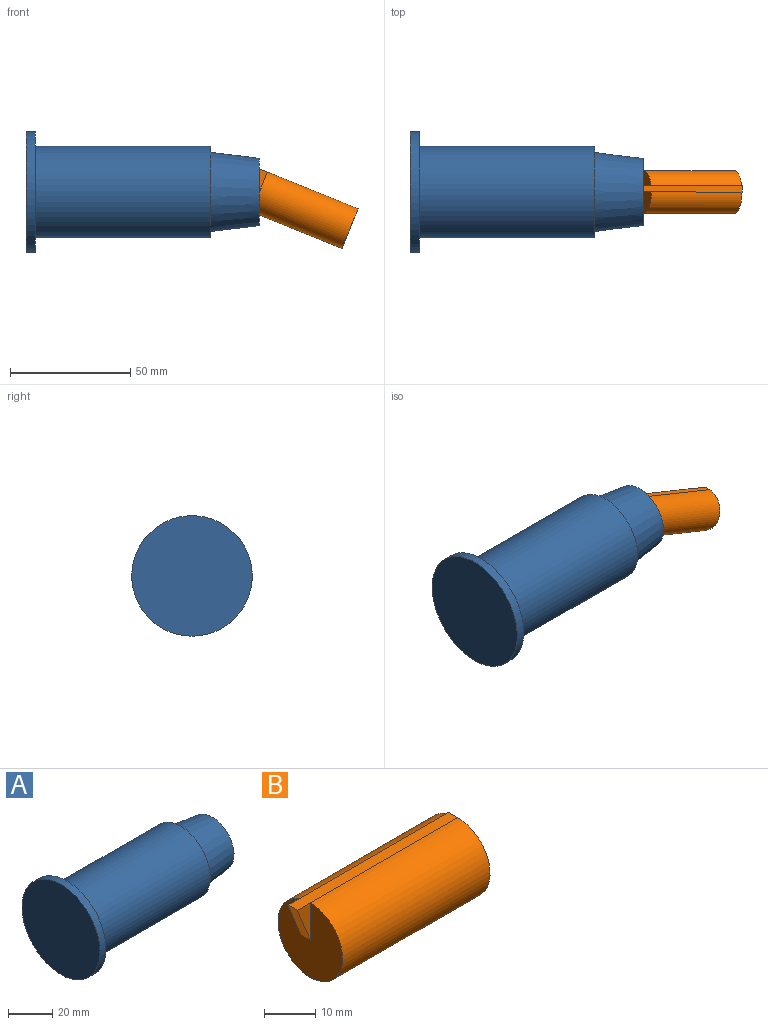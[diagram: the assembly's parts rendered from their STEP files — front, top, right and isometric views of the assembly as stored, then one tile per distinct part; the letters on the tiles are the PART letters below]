
ASSEMBLY  parts=2 mates=1
PART A: 7 faces, bbox 97.2x50.1x50.1 mm
  f0: plane 27.94x27.94mm, normal (1,0,0), area 613.1mm2, adj f1
  f1: cone r=13.97mm half-angle=7.1deg, axis (-1,0,0), area 1960.9mm2, adj f0,f2
  f2: plane 38.1x38.1mm, normal (1,0,0), area 283.8mm2, adj f1,f3
  f3: cylinder r=19.05mm len=73.03mm, axis (1,0,0), area 8740.7mm2, adj f2,f4
  f4: plane 50.14x50.14mm, normal (1,0,0), area 834.4mm2, adj f3,f5
  f5: cylinder r=25.07mm len=50.14mm, axis (1,0,0), area 600.1mm2, adj f4,f6
  f6: plane 50.14x50.14mm, normal (-1,0,0), area 1974.5mm2, adj f5
PART B: 7 faces, bbox 44.2x17.8x17.8 mm
  f0: cylinder r=8.89mm len=40.64mm, axis (-1,0,0), area 2165.4mm2, adj f1,f2,f3,f5
  f1: plane 17.78x17.78mm, normal (-1,0,0), area 226mm2, adj f0,f4,f5,f6
  f2: plane 17.78x17.78mm, normal (1,0,0), area 248.6mm2, adj f0,f3,f5
  f3: plane 44.23x2.54mm, normal (0,0,1), area 112.3mm2, adj f0,f2,f4,f5,f6
  f4: plane 8.89x3.59mm, normal (-0.93,0,-0.37), area 24.4mm2, adj f1,f3,f5,f6
  f5: plane 44.23x8.89mm, normal (0,1,0), area 31mm2, adj f0,f1,f2,f3,f4
  f6: plane 8.89x3.59mm, normal (0,-1,0), area 16mm2, adj f1,f3,f4
PLACE A t=(-62.23,-16.95,-13.6)mm
PLACE B rot(axis=(0,1,0),22deg) t=(34.92,-16.95,-13.6)mm
MATE fastened B.f4 <-> A.f1  axis (-1,0,0) through (34.92,-16.95,-13.6)mm
